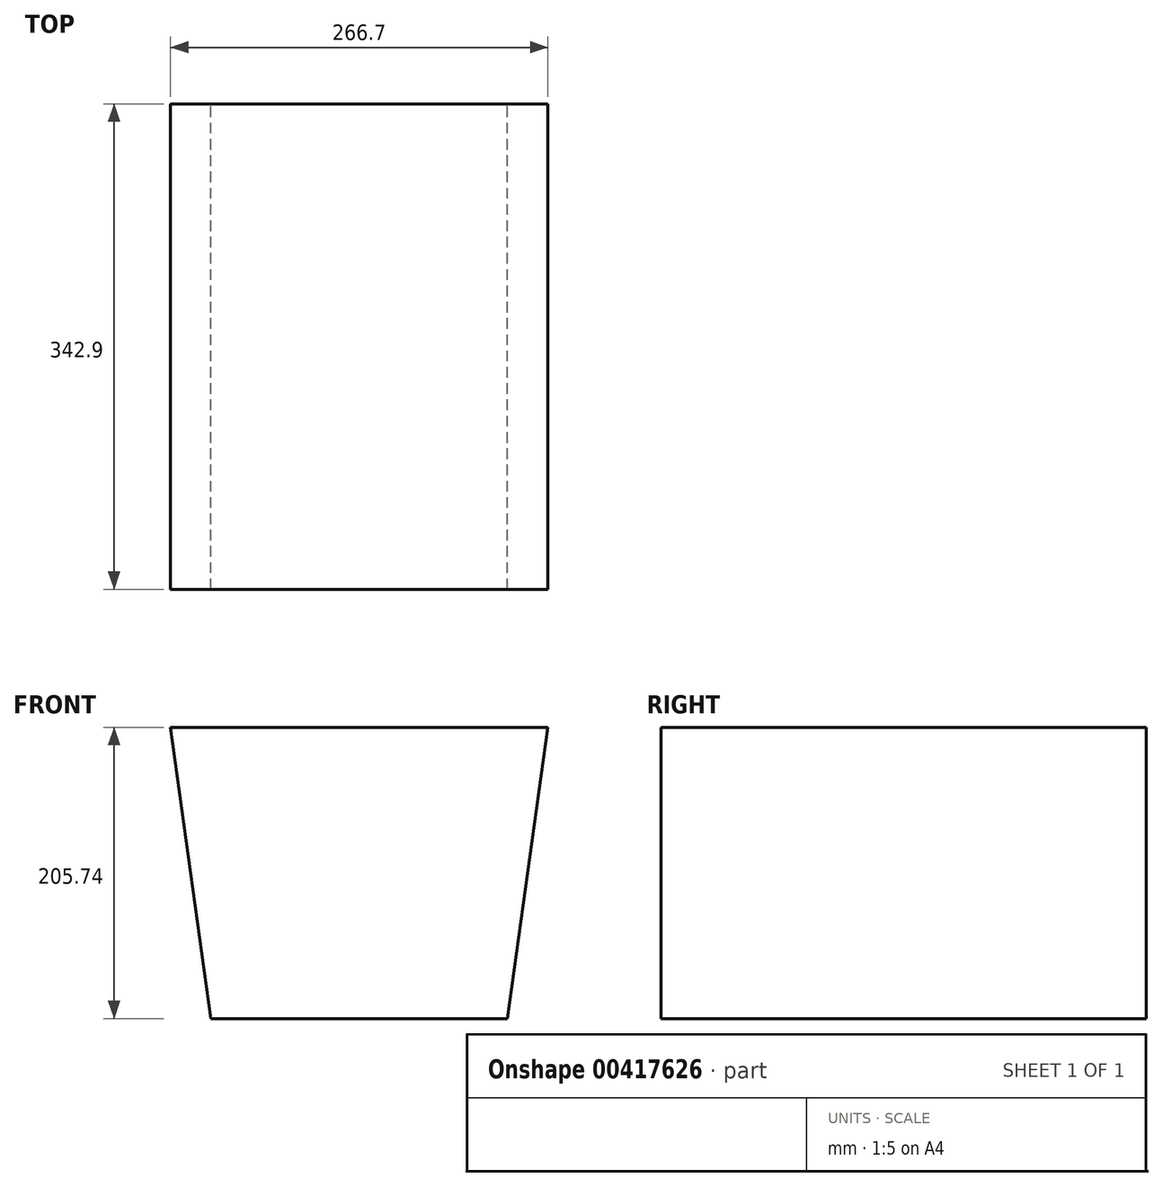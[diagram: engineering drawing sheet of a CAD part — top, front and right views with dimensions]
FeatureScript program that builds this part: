
annotation { "Feature Type Name" : "Feature", "Feature Type Description" : "" }
export const myFeature = defineFeature(function(context is Context, id is Id, definition is map)
    precondition{}
    {
        {
            var Q0;
            Q0=qCreatedBy(makeId("Front.planeOp"),FACE);
            var sketch = newSketch(context, id + "F0", { "sketchPlane" : qUnion([Q0])});
            skLineSegment(sketch, "E0", {"start": v(-104.78, 0) * mm, "end": v(104.78, 0) * mm});
            skLineSegment(sketch, "E1", {"start": v(-133.35, 205.74) * mm, "end": v(133.35, 205.74) * mm});
            skLineSegment(sketch, "E2", {"start": v(-104.78, 0) * mm, "end": v(-133.35, 205.74) * mm});
            skLineSegment(sketch, "E3", {"start": v(104.78, 0) * mm, "end": v(133.35, 205.74) * mm});
            skSolve(sketch);
        }
        {
            var Q0;
            Q0=makeQuery(id+"F0.imprint","IMPRINT",FACE,{"disambiguationData":[TD([[makeQuery(id+"F0.imprint","IMPRINT",EDGE,{"derivedFrom":sQuery(id+"F0.wireOp",EDGE,"E0")}),1.0]])]});
            extrude(context, id + "F1", {"entities" : qUnion([Q0]), "depth" : 342.9 * mm});
        }
    });
